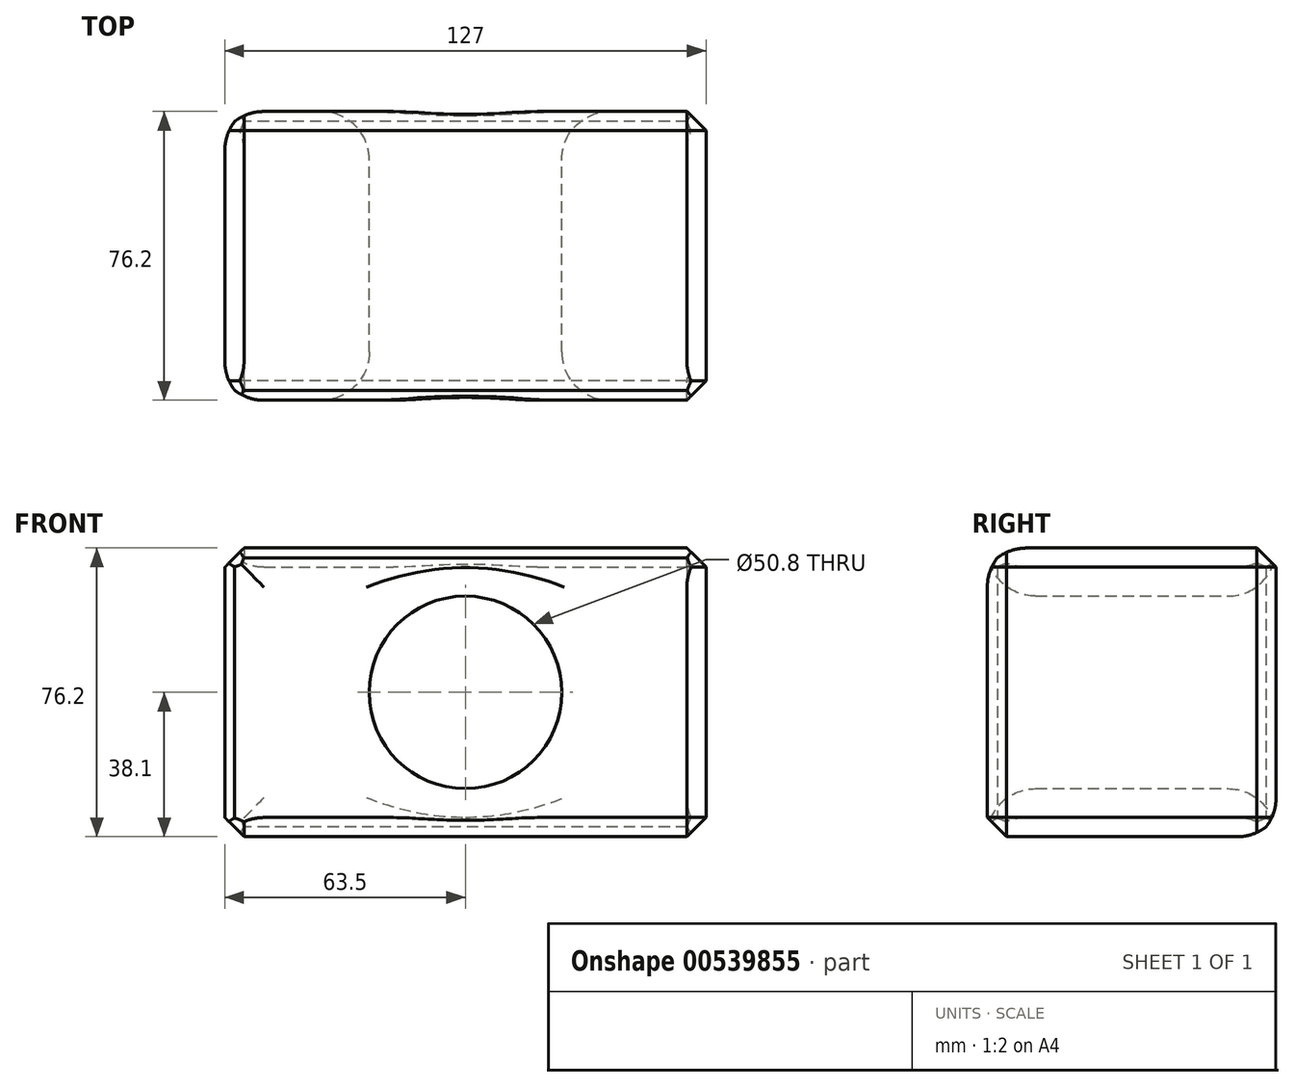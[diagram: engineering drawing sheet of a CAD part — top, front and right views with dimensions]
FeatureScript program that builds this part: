
annotation { "Feature Type Name" : "Feature", "Feature Type Description" : "" }
export const myFeature = defineFeature(function(context is Context, id is Id, definition is map)
    precondition{}
    {
        {
            var Q0;
            Q0=qCreatedBy(makeId("Front.planeOp"),FACE);
            var sketch = newSketch(context, id + "F0", { "sketchPlane" : qUnion([Q0])});
            skLineSegment(sketch, "E0.bottom", {"start": v(-63.5, 38.1) * mm, "end": v(63.5, 38.1) * mm});
            skLineSegment(sketch, "E0.top", {"start": v(-63.5, -38.1) * mm, "end": v(63.5, -38.1) * mm});
            skLineSegment(sketch, "E0.left", {"start": v(-63.5, 38.1) * mm, "end": v(-63.5, -38.1) * mm});
            skLineSegment(sketch, "E0.right", {"start": v(63.5, 38.1) * mm, "end": v(63.5, -38.1) * mm});
            skPoint(sketch, "E0.middle", {"position": v(0, 0) * mm});
            skCircle(sketch, "E1", {"center": v(0, 0) * mm, "radius": 25.4 * mm});
            skSolve(sketch);
        }
        {
            var Q0;
            Q0 = qSketchRegion(id + "F0", true);
            extrude(context, id + "F1", {"entities" : qUnion([Q0]), "depth" : 76.2 * mm, "offsetDistance" : 25.4 * mm});
        }
        {
            var Q0;
            Q0=makeQuery(id+"F1.opExtrude","CAP_EDGE",EDGE,{"disambiguationData":[OSD([sQuery(id+"F0.wireOp",EDGE,"E0.bottom")])],"isStart":false});
            var Q1;
            Q1=makeQuery(id+"F1.opExtrude","SWEPT_EDGE",EDGE,{"disambiguationData":[OSD([sQuery(id+"F0.wireOp",EDGE,"E0.bottom"),sQuery(id+"F0.wireOp",EDGE,"E0.left")])]});
            var Q2;
            Q2=makeQuery(id+"F1.opExtrude","CAP_EDGE",EDGE,{"disambiguationData":[OSD([sQuery(id+"F0.wireOp",EDGE,"E0.bottom")])],"isStart":true});
            var Q3;
            Q3=makeQuery(id+"F1.opExtrude","SWEPT_EDGE",EDGE,{"disambiguationData":[OSD([sQuery(id+"F0.wireOp",EDGE,"E0.bottom"),sQuery(id+"F0.wireOp",EDGE,"E0.right")])]});
            var Q4;
            Q4=makeQuery(id+"F1.opExtrude","CAP_EDGE",EDGE,{"disambiguationData":[OSD([sQuery(id+"F0.wireOp",EDGE,"E0.right")])],"isStart":false});
            var Q5;
            Q5=makeQuery(id+"F1.opExtrude","CAP_EDGE",EDGE,{"disambiguationData":[OSD([sQuery(id+"F0.wireOp",EDGE,"E0.top")])],"isStart":false});
            var Q6;
            Q6=makeQuery(id+"F1.opExtrude","CAP_EDGE",EDGE,{"disambiguationData":[OSD([sQuery(id+"F0.wireOp",EDGE,"E0.left")])],"isStart":false});
            var Q7;
            Q7=makeQuery(id+"F1.opExtrude","SWEPT_EDGE",EDGE,{"disambiguationData":[OSD([sQuery(id+"F0.wireOp",EDGE,"E0.top"),sQuery(id+"F0.wireOp",EDGE,"E0.right")])]});
            var Q8;
            Q8=makeQuery(id+"F1.opExtrude","SWEPT_FACE",FACE,{"disambiguationData":[OSD([sQuery(id+"F0.wireOp",EDGE,"E0.right")])]});
            var Q9;
            Q9=makeQuery(id+"F1.opExtrude","CAP_EDGE",EDGE,{"disambiguationData":[OSD([sQuery(id+"F0.wireOp",EDGE,"E0.top")])],"isStart":true});
            var Q10;
            Q10=makeQuery(id+"F1.opExtrude","CAP_EDGE",EDGE,{"disambiguationData":[OSD([sQuery(id+"F0.wireOp",EDGE,"E0.left")])],"isStart":true});
            var Q11;
            Q11=makeQuery(id+"F1.opExtrude","SWEPT_EDGE",EDGE,{"disambiguationData":[OSD([sQuery(id+"F0.wireOp",EDGE,"E0.top"),sQuery(id+"F0.wireOp",EDGE,"E0.left")])]});
            chamfer(context, id + "F2", {"entities" : qUnion([Q0, Q1, Q2, Q3, Q4, Q5, Q6, Q7, Q8, Q9, Q10, Q11]), "width" : 5.08 * mm, "tangentPropagation" : true});
        }
        {
            var Q0;
            Q0=makeQuery(id+"F1.opExtrude","CAP_EDGE",EDGE,{"disambiguationData":[OSD([sQuery(id+"F0.wireOp",EDGE,"E1")])],"isStart":false});
            var Q1;
            Q1=makeQuery(id+"F1.opExtrude","CAP_EDGE",EDGE,{"disambiguationData":[OSD([sQuery(id+"F0.wireOp",EDGE,"E1")])],"isStart":true});
            var Q2;
            {var subQ0=sQuery(id+"F0.wireOp",EDGE,"E0.top");Q2=makeQuery(id+"F2.opChamfer","BLEND_EDGE",EDGE,{"blendedFrom":[makeQuery(id+"F1.opExtrude","CAP_EDGE",EDGE,{"disambiguationData":[OSD([subQ0])],"isStart":true}),makeQuery(id+"F1.opExtrude","CAP_FACE",FACE,{"disambiguationData":[OSD([sQuery(id+"F0.wireOp",EDGE,"E0.bottom"),subQ0,sQuery(id+"F0.wireOp",EDGE,"E0.left"),sQuery(id+"F0.wireOp",EDGE,"E0.right"),sQuery(id+"F0.wireOp",EDGE,"E1")])],"isStart":true})],"blendedInto":[makeQuery(id+"F1.opExtrude","CAP_FACE",FACE,{"disambiguationData":[OSD([sQuery(id+"F0.wireOp",EDGE,"E0.bottom"),subQ0,sQuery(id+"F0.wireOp",EDGE,"E0.left"),sQuery(id+"F0.wireOp",EDGE,"E0.right"),sQuery(id+"F0.wireOp",EDGE,"E1")])],"isStart":true})]});}
            var Q3;
            {var subQ0=sQuery(id+"F0.wireOp",EDGE,"E0.top");Q3=makeQuery(id+"F2.opChamfer","BLEND_EDGE",EDGE,{"blendedFrom":[makeQuery(id+"F1.opExtrude","CAP_EDGE",EDGE,{"disambiguationData":[OSD([subQ0])],"isStart":true}),makeQuery(id+"F1.opExtrude","SWEPT_FACE",FACE,{"disambiguationData":[OSD([subQ0])]})],"blendedInto":[makeQuery(id+"F1.opExtrude","SWEPT_FACE",FACE,{"disambiguationData":[OSD([subQ0])]})]});}
            var Q4;
            {var subQ0=sQuery(id+"F0.wireOp",EDGE,"E0.bottom");Q4=makeQuery(id+"F2.opChamfer","BLEND_EDGE",EDGE,{"blendedFrom":[makeQuery(id+"F1.opExtrude","CAP_EDGE",EDGE,{"disambiguationData":[OSD([subQ0])],"isStart":false}),makeQuery(id+"F1.opExtrude","SWEPT_FACE",FACE,{"disambiguationData":[OSD([subQ0])]})],"blendedInto":[makeQuery(id+"F1.opExtrude","SWEPT_FACE",FACE,{"disambiguationData":[OSD([subQ0])]})]});}
            var Q5;
            {var subQ0=sQuery(id+"F0.wireOp",EDGE,"E0.left");Q5=makeQuery(id+"F2.opChamfer","BLEND_EDGE",EDGE,{"blendedFrom":[makeQuery(id+"F1.opExtrude","CAP_EDGE",EDGE,{"disambiguationData":[OSD([subQ0])],"isStart":false}),makeQuery(id+"F1.opExtrude","SWEPT_FACE",FACE,{"disambiguationData":[OSD([subQ0])]})],"blendedInto":[makeQuery(id+"F1.opExtrude","SWEPT_FACE",FACE,{"disambiguationData":[OSD([subQ0])]})]});}
            var Q6;
            {var subQ0=sQuery(id+"F0.wireOp",EDGE,"E0.left");Q6=makeQuery(id+"F2.opChamfer","BLEND_EDGE",EDGE,{"blendedFrom":[makeQuery(id+"F1.opExtrude","CAP_EDGE",EDGE,{"disambiguationData":[OSD([subQ0])],"isStart":false}),makeQuery(id+"F1.opExtrude","CAP_FACE",FACE,{"disambiguationData":[OSD([sQuery(id+"F0.wireOp",EDGE,"E0.bottom"),sQuery(id+"F0.wireOp",EDGE,"E0.top"),subQ0,sQuery(id+"F0.wireOp",EDGE,"E0.right"),sQuery(id+"F0.wireOp",EDGE,"E1")])],"isStart":false})],"blendedInto":[makeQuery(id+"F1.opExtrude","CAP_FACE",FACE,{"disambiguationData":[OSD([sQuery(id+"F0.wireOp",EDGE,"E0.bottom"),sQuery(id+"F0.wireOp",EDGE,"E0.top"),subQ0,sQuery(id+"F0.wireOp",EDGE,"E0.right"),sQuery(id+"F0.wireOp",EDGE,"E1")])],"isStart":false})]});}
            var Q7;
            {var subQ0=sQuery(id+"F0.wireOp",EDGE,"E0.bottom");Q7=makeQuery(id+"F2.opChamfer","BLEND_EDGE",EDGE,{"blendedFrom":[makeQuery(id+"F1.opExtrude","CAP_EDGE",EDGE,{"disambiguationData":[OSD([subQ0])],"isStart":false}),makeQuery(id+"F1.opExtrude","CAP_FACE",FACE,{"disambiguationData":[OSD([subQ0,sQuery(id+"F0.wireOp",EDGE,"E0.top"),sQuery(id+"F0.wireOp",EDGE,"E0.left"),sQuery(id+"F0.wireOp",EDGE,"E0.right"),sQuery(id+"F0.wireOp",EDGE,"E1")])],"isStart":false})],"blendedInto":[makeQuery(id+"F1.opExtrude","CAP_FACE",FACE,{"disambiguationData":[OSD([subQ0,sQuery(id+"F0.wireOp",EDGE,"E0.top"),sQuery(id+"F0.wireOp",EDGE,"E0.left"),sQuery(id+"F0.wireOp",EDGE,"E0.right"),sQuery(id+"F0.wireOp",EDGE,"E1")])],"isStart":false})]});}
            var Q8;
            {var subQ0=sQuery(id+"F0.wireOp",EDGE,"E0.left");Q8=makeQuery(id+"F2.opChamfer","BLEND_EDGE",EDGE,{"blendedFrom":[makeQuery(id+"F1.opExtrude","CAP_EDGE",EDGE,{"disambiguationData":[OSD([subQ0])],"isStart":true}),makeQuery(id+"F1.opExtrude","SWEPT_FACE",FACE,{"disambiguationData":[OSD([subQ0])]})],"blendedInto":[makeQuery(id+"F1.opExtrude","SWEPT_FACE",FACE,{"disambiguationData":[OSD([subQ0])]})]});}
            var Q9;
            {var subQ0=sQuery(id+"F0.wireOp",EDGE,"E0.left");Q9=makeQuery(id+"F2.opChamfer","BLEND_EDGE",EDGE,{"blendedFrom":[makeQuery(id+"F1.opExtrude","CAP_EDGE",EDGE,{"disambiguationData":[OSD([subQ0])],"isStart":true}),makeQuery(id+"F1.opExtrude","CAP_FACE",FACE,{"disambiguationData":[OSD([sQuery(id+"F0.wireOp",EDGE,"E0.bottom"),sQuery(id+"F0.wireOp",EDGE,"E0.top"),subQ0,sQuery(id+"F0.wireOp",EDGE,"E0.right"),sQuery(id+"F0.wireOp",EDGE,"E1")])],"isStart":true})],"blendedInto":[makeQuery(id+"F1.opExtrude","CAP_FACE",FACE,{"disambiguationData":[OSD([sQuery(id+"F0.wireOp",EDGE,"E0.bottom"),sQuery(id+"F0.wireOp",EDGE,"E0.top"),subQ0,sQuery(id+"F0.wireOp",EDGE,"E0.right"),sQuery(id+"F0.wireOp",EDGE,"E1")])],"isStart":true})]});}
            fillet(context, id + "F3", {"entities" : qUnion([Q0, Q1, Q2, Q3, Q4, Q5, Q6, Q7, Q8, Q9]), "radius" : 12.7 * mm, "tangentPropagation" : true, "allowEdgeOverflow" : false});
        }
    });
